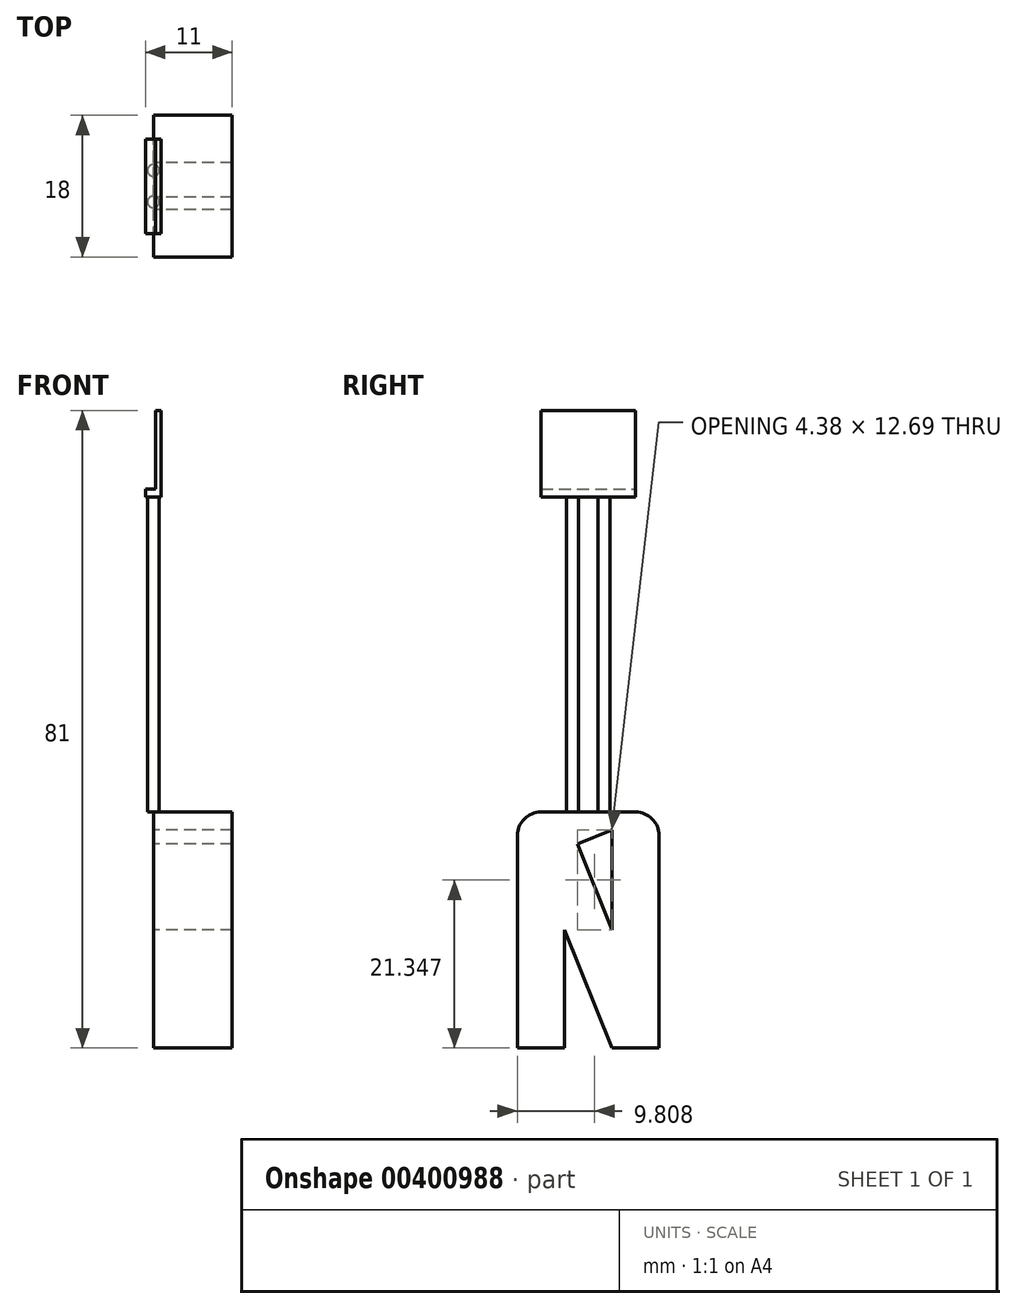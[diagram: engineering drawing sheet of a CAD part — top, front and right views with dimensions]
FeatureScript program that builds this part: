
annotation { "Feature Type Name" : "Feature", "Feature Type Description" : "" }
export const myFeature = defineFeature(function(context is Context, id is Id, definition is map)
    precondition{}
    {
        {
            var Q0;
            Q0=qCreatedBy(makeId("Right.planeOp"),FACE);
            var sketch = newSketch(context, id + "F0", { "sketchPlane" : qUnion([Q0])});
            skLineSegment(sketch, "E0.bottom", {"start": v(-14.05, 13.77) * mm, "end": v(-8.05, 13.77) * mm});
            skLineSegment(sketch, "E0.top", {"start": v(-14.05, -16.23) * mm, "end": v(-8.05, -16.23) * mm});
            skLineSegment(sketch, "E0.left", {"start": v(-14.05, 13.77) * mm, "end": v(-14.05, -16.23) * mm});
            skLineSegment(sketch, "E0.right", {"start": v(-8.05, 13.77) * mm, "end": v(-8.05, -16.23) * mm});
            skLineSegment(sketch, "E1.bottom", {"start": v(-2.05, 13.77) * mm, "end": v(3.95, 13.77) * mm});
            skLineSegment(sketch, "E1.top", {"start": v(-2.05, -16.23) * mm, "end": v(3.95, -16.23) * mm});
            skLineSegment(sketch, "E1.left", {"start": v(3.95, 13.77) * mm, "end": v(3.95, -16.23) * mm});
            skLineSegment(sketch, "E1.right", {"start": v(-2.05, 13.77) * mm, "end": v(-2.05, -16.23) * mm});
            skLineSegment(sketch, "E2", {"start": v(3.95, 12.58) * mm, "end": v(3.95, 13.77) * mm});
            skLineSegment(sketch, "E3", {"start": v(-8.05, 13.77) * mm, "end": v(3.95, -16.23) * mm});
            skLineSegment(sketch, "E4", {"start": v(-2.05, -16.23) * mm, "end": v(-14.05, 13.77) * mm});
            skLineSegment(sketch, "E5", {"start": v(-2.05, 13.77) * mm, "end": v(-8.05, 13.77) * mm});
            skLineSegment(sketch, "E6", {"start": v(-6.43, 9.71) * mm, "end": v(-2.05, 11.46) * mm});
            skSolve(sketch);
        }
        {
            var Q0;
            {var subQ0=sQuery(id+"F0.wireOp",EDGE,"E5");Q0=makeQuery(id+"F0.imprint","IMPRINT",FACE,{"disambiguationData":[TD([[makeQuery(id+"F0.imprint","IMPRINT",EDGE,{"derivedFrom":subQ0}),1.0]])]});}
            var Q1;
            {var subQ4=sQuery(id+"F0.wireOp",EDGE,"E1.bottom");Q1=makeQuery(id+"F0.imprint","IMPRINT",FACE,{"disambiguationData":[TD([[makeQuery(id+"F0.imprint","IMPRINT",EDGE,{"derivedFrom":subQ4}),-1.0]])]});}
            var Q2;
            {var subQ0=sQuery(id+"F0.wireOp",EDGE,"E1.top");Q2=makeQuery(id+"F0.imprint","IMPRINT",FACE,{"disambiguationData":[TD([[makeQuery(id+"F0.imprint","IMPRINT",EDGE,{"derivedFrom":subQ0}),1.0]])]});}
            var Q3;
            {var subQ0=sQuery(id+"F0.wireOp",EDGE,"E3");var subQ3=makeQuery(id+"F0.imprint","INTERSECT",VERTEX,{"derivedFrom":[subQ0,sQuery(id+"F0.wireOp",EDGE,"E6")]});Q3=makeQuery(id+"F0.imprint","IMPRINT",FACE,{"disambiguationData":[TD([[makeQuery(id+"F0.imprint","IMPRINT",EDGE,{"disambiguationData":[TD([[subQ3,-1.0]])],"derivedFrom":subQ0}),-1.0]])]});}
            var Q4;
            {var subQ0=sQuery(id+"F0.wireOp",EDGE,"E0.bottom");Q4=makeQuery(id+"F0.imprint","IMPRINT",FACE,{"disambiguationData":[TD([[makeQuery(id+"F0.imprint","IMPRINT",EDGE,{"derivedFrom":subQ0}),-1.0]])]});}
            var Q5;
            {var subQ0=sQuery(id+"F0.wireOp",EDGE,"E0.top");Q5=makeQuery(id+"F0.imprint","IMPRINT",FACE,{"disambiguationData":[TD([[makeQuery(id+"F0.imprint","IMPRINT",EDGE,{"derivedFrom":subQ0}),1.0]])]});}
            extrude(context, id + "F1", {"entities" : qUnion([Q0, Q1, Q2, Q3, Q4, Q5]), "depth" : 10 * mm});
        }
        {
            var Q0;
            Q0=makeQuery(id+"F1.opExtrude","SWEPT_EDGE",EDGE,{"disambiguationData":[OSD([sQuery(id+"F0.wireOp",EDGE,"E0.bottom"),sQuery(id+"F0.wireOp",EDGE,"E0.left"),sQuery(id+"F0.wireOp",EDGE,"E4")])]});
            fillet(context, id + "F2", {"entities" : qUnion([Q0]), "radius" : 3 * mm, "tangentPropagation" : true, "allowEdgeOverflow" : false});
        }
        {
            var Q0;
            Q0=makeQuery(id+"F1.opExtrude","SWEPT_EDGE",EDGE,{"disambiguationData":[OSD([sQuery(id+"F0.wireOp",EDGE,"E1.bottom"),sQuery(id+"F0.wireOp",EDGE,"E2")])]});
            fillet(context, id + "F3", {"entities" : qUnion([Q0]), "radius" : 3 * mm, "tangentPropagation" : true, "allowEdgeOverflow" : false});
        }
        {
            var Q0;
            Q0=makeQuery(id+"F1.opExtrude","SWEPT_FACE",FACE,{"disambiguationData":[OSD([sQuery(id+"F0.wireOp",EDGE,"E0.bottom"),sQuery(id+"F0.wireOp",EDGE,"E1.bottom"),sQuery(id+"F0.wireOp",EDGE,"E5")])]});
            var sketch = newSketch(context, id + "F4", { "sketchPlane" : qUnion([Q0])});
            skCircle(sketch, "E7", {"center": v(0, -3.05) * mm, "radius": 0.75 * mm});
            skCircle(sketch, "E8", {"center": v(0, -7.05) * mm, "radius": 0.75 * mm});
            skSolve(sketch);
        }
        {
            var Q0;
            {var subQ0=sQuery(id+"F4.wireOp",EDGE,"E7");var subQ1=makeQuery(id+"F1.opExtrude","CAP_EDGE",EDGE,{"disambiguationData":[OSD([sQuery(id+"F0.wireOp",EDGE,"E0.bottom"),sQuery(id+"F0.wireOp",EDGE,"E1.bottom"),sQuery(id+"F0.wireOp",EDGE,"E5")])],"isStart":true});var subQ2=makeQuery(id+"F4.imprint","INTERSECT",VERTEX,{"disambiguationData":[OD(0.0)],"derivedFrom":[subQ1,subQ0]});Q0=makeQuery(id+"F4.imprint","IMPRINT",FACE,{"disambiguationData":[TD([[makeQuery(id+"F4.imprint","IMPRINT",EDGE,{"disambiguationData":[TD([[subQ2,-1.0]])],"derivedFrom":subQ0}),1.0]])]});}
            var Q1;
            {var subQ0=sQuery(id+"F4.wireOp",EDGE,"E7");var subQ1=makeQuery(id+"F1.opExtrude","CAP_EDGE",EDGE,{"disambiguationData":[OSD([sQuery(id+"F0.wireOp",EDGE,"E0.bottom"),sQuery(id+"F0.wireOp",EDGE,"E1.bottom"),sQuery(id+"F0.wireOp",EDGE,"E5")])],"isStart":true});var subQ2=makeQuery(id+"F4.imprint","INTERSECT",VERTEX,{"disambiguationData":[OD(0.0)],"derivedFrom":[subQ1,subQ0]});Q1=makeQuery(id+"F4.imprint","IMPRINT",FACE,{"disambiguationData":[TD([[makeQuery(id+"F4.imprint","IMPRINT",EDGE,{"disambiguationData":[TD([[subQ2,1.0]])],"derivedFrom":subQ0}),1.0]])]});}
            var Q2;
            {var subQ0=sQuery(id+"F4.wireOp",EDGE,"E8");var subQ1=makeQuery(id+"F1.opExtrude","CAP_EDGE",EDGE,{"disambiguationData":[OSD([sQuery(id+"F0.wireOp",EDGE,"E0.bottom"),sQuery(id+"F0.wireOp",EDGE,"E1.bottom"),sQuery(id+"F0.wireOp",EDGE,"E5")])],"isStart":true});var subQ2=makeQuery(id+"F4.imprint","INTERSECT",VERTEX,{"disambiguationData":[OD(0.0)],"derivedFrom":[subQ1,subQ0]});Q2=makeQuery(id+"F4.imprint","IMPRINT",FACE,{"disambiguationData":[TD([[makeQuery(id+"F4.imprint","IMPRINT",EDGE,{"disambiguationData":[TD([[subQ2,-1.0]])],"derivedFrom":subQ0}),1.0]])]});}
            var Q3;
            {var subQ0=sQuery(id+"F4.wireOp",EDGE,"E8");var subQ1=makeQuery(id+"F1.opExtrude","CAP_EDGE",EDGE,{"disambiguationData":[OSD([sQuery(id+"F0.wireOp",EDGE,"E0.bottom"),sQuery(id+"F0.wireOp",EDGE,"E1.bottom"),sQuery(id+"F0.wireOp",EDGE,"E5")])],"isStart":true});var subQ2=makeQuery(id+"F4.imprint","INTERSECT",VERTEX,{"disambiguationData":[OD(0.0)],"derivedFrom":[subQ1,subQ0]});Q3=makeQuery(id+"F4.imprint","IMPRINT",FACE,{"disambiguationData":[TD([[makeQuery(id+"F4.imprint","IMPRINT",EDGE,{"disambiguationData":[TD([[subQ2,1.0]])],"derivedFrom":subQ0}),1.0]])]});}
            extrude(context, id + "F5", {"entities" : qUnion([Q0, Q1, Q2, Q3]), "operationType" : NewBodyOperationType.ADD, "depth" : 40 * mm});
        }
        {
            var Q0;
            Q0=makeQuery(id+"F5.opExtrude","CAP_FACE",FACE,{"disambiguationData":[OSD([sQuery(id+"F4.wireOp",EDGE,"E8")])],"isStart":false});
            var sketch = newSketch(context, id + "F6", { "sketchPlane" : qUnion([Q0])});
            skLineSegment(sketch, "E9.bottom", {"start": v(-1, 0.95) * mm, "end": v(1, 0.95) * mm});
            skLineSegment(sketch, "E9.top", {"start": v(-1, -11.05) * mm, "end": v(1, -11.05) * mm});
            skLineSegment(sketch, "E9.left", {"start": v(-1, 0.95) * mm, "end": v(-1, -11.05) * mm});
            skLineSegment(sketch, "E9.right", {"start": v(1, 0.95) * mm, "end": v(1, -11.05) * mm});
            skPoint(sketch, "E9.middle", {"position": v(0, -5.05) * mm});
            skSolve(sketch);
        }
        {
            var Q0;
            Q0 = qSketchRegion(id + "F6", true);
            extrude(context, id + "F7", {"entities" : qUnion([Q0]), "operationType" : NewBodyOperationType.ADD, "depth" : 1 * mm});
        }
        {
            var Q0;
            Q0=makeQuery(id+"F7.opExtrude","CAP_FACE",FACE,{"disambiguationData":[OSD([sQuery(id+"F6.wireOp",EDGE,"E9.bottom"),sQuery(id+"F6.wireOp",EDGE,"E9.top"),sQuery(id+"F6.wireOp",EDGE,"E9.left"),sQuery(id+"F6.wireOp",EDGE,"E9.right")])],"isStart":false});
            var sketch = newSketch(context, id + "F8", { "sketchPlane" : qUnion([Q0])});
            skLineSegment(sketch, "E10", {"start": v(0.25, -11.05) * mm, "end": v(0.25, 0.95) * mm});
            skSolve(sketch);
        }
        {
            var Q0;
            {var subQ0=sQuery(id+"F8.wireOp",EDGE,"E10");Q0=makeQuery(id+"F8.imprint","IMPRINT",FACE,{"disambiguationData":[TD([[makeQuery(id+"F8.imprint","IMPRINT",EDGE,{"derivedFrom":subQ0}),-1.0]])]});}
            extrude(context, id + "F9", {"entities" : qUnion([Q0]), "operationType" : NewBodyOperationType.ADD, "depth" : 10 * mm});
        }
    });
